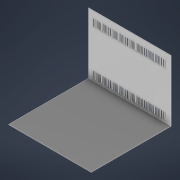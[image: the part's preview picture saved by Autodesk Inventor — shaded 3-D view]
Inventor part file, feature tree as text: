
AUTODESK INVENTOR PART (.ipt)
format: ipt  version: 2022 (Build 260153070, 153G)  size: 810,496 bytes
history: native  units: mm
features: extrude x2, chamfer x2, other x2, sketch x2
ambient origin geometry x8: Origin, YZ Plane, XZ Plane, XY Plane, X Axis, Y Axis, Z Axis, Center Point
bodies: Body1 (feature_tree)
feature tree (8):
  extrude  "Выдавливание2"  Depth=3.0mm
  chamfer  "Фаска1"  Distance=218.0mm
  chamfer  "Фаска2"  Distance=163.0mm
  other  "Определение главной стороны"
  extrude  "Выдавливание3"  Depth=5.0mm
  sketch  "Эскиз2"
  sketch  "Эскиз3"
  other  "Определение1"
